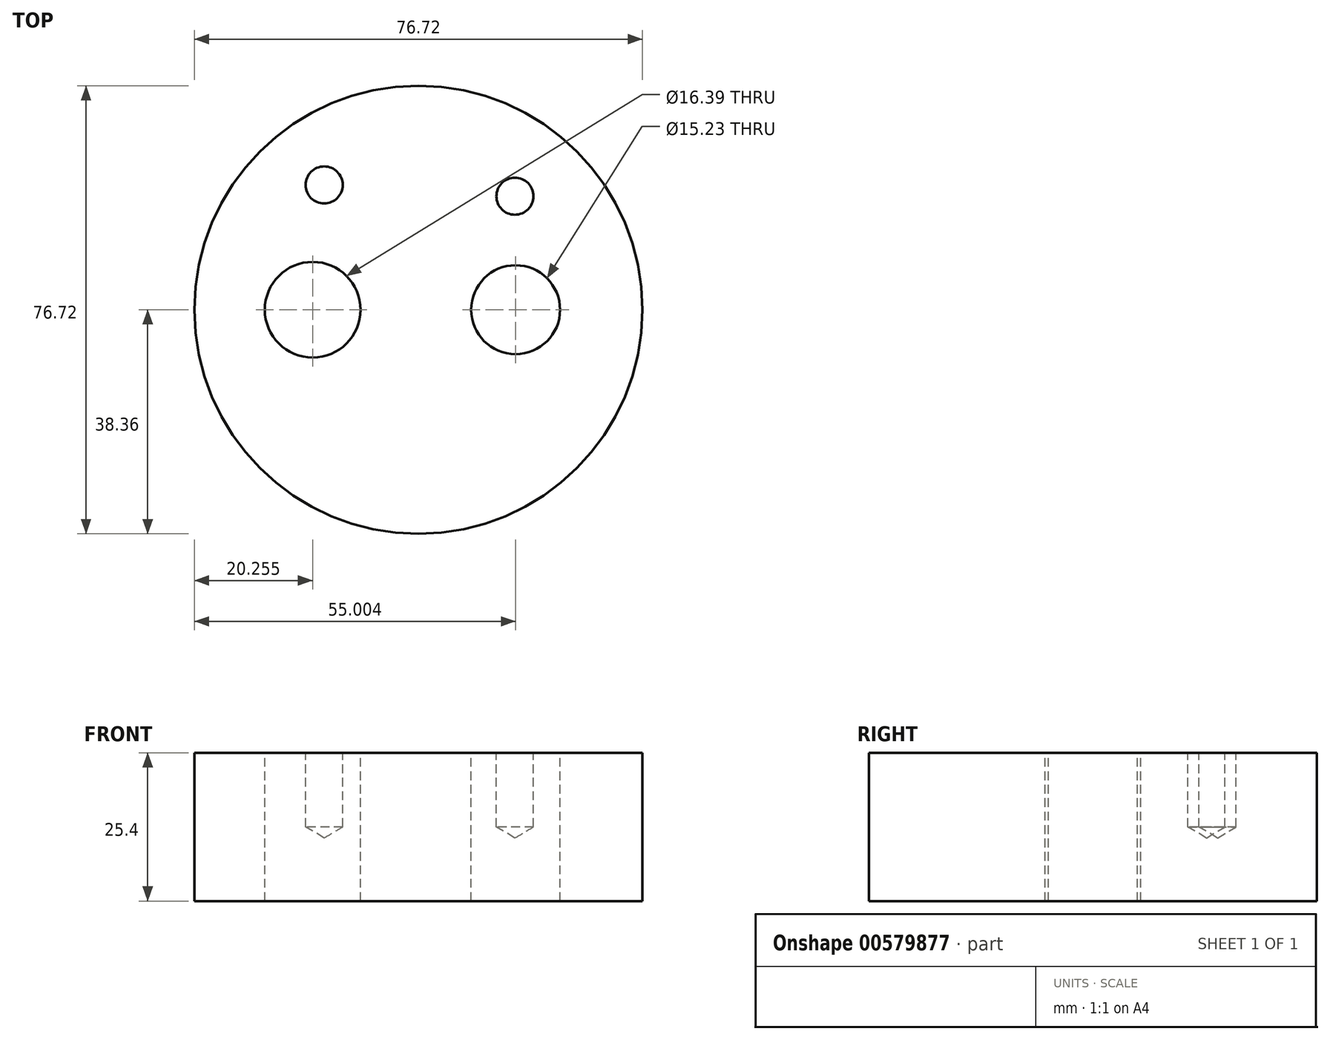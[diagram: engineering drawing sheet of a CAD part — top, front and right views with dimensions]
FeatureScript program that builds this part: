
annotation { "Feature Type Name" : "Feature", "Feature Type Description" : "" }
export const myFeature = defineFeature(function(context is Context, id is Id, definition is map)
    precondition{}
    {
        {
            var Q0;
            Q0=qCreatedBy(makeId("Top.planeOp"),FACE);
            var sketch = newSketch(context, id + "F0", { "sketchPlane" : qUnion([Q0])});
            skCircle(sketch, "E0", {"center": v(0, 0) * mm, "radius": 38.36 * mm});
            skSolve(sketch);
        }
        {
            var Q0;
            Q0 = qSketchRegion(id + "F0", true);
            extrude(context, id + "F1", {"entities" : qUnion([Q0]), "depth" : 25.4 * mm, "offsetDistance" : 25.4 * mm});
        }
        {
            var Q0;
            Q0=makeQuery(id+"F1.opExtrude","CAP_FACE",FACE,{"disambiguationData":[OSD([sQuery(id+"F0.wireOp",EDGE,"E0")])],"isStart":false});
            var sketch = newSketch(context, id + "F2", { "sketchPlane" : qUnion([Q0])});
            skCircle(sketch, "E1", {"center": v(-18.1, 0) * mm, "radius": 8.2 * mm});
            skCircle(sketch, "E2", {"center": v(16.64, 0) * mm, "radius": 7.61 * mm});
            skSolve(sketch);
        }
        {
            var Q0;
            Q0=makeQuery(id+"F2.imprint","IMPRINT",FACE,{"disambiguationData":[TD([[makeQuery(id+"F2.imprint","IMPRINT",EDGE,{"derivedFrom":sQuery(id+"F2.wireOp",EDGE,"E2")}),1.0]])]});
            var Q1;
            Q1=makeQuery(id+"F2.imprint","IMPRINT",FACE,{"disambiguationData":[TD([[makeQuery(id+"F2.imprint","IMPRINT",EDGE,{"derivedFrom":sQuery(id+"F2.wireOp",EDGE,"E1")}),1.0]])]});
            extrude(context, id + "F3", {"entities" : qUnion([Q0, Q1]), "operationType" : NewBodyOperationType.REMOVE, "endBound" : BoundingType.THROUGH_ALL, "oppositeDirection" : true, "depth" : 25.4 * mm, "offsetDistance" : 25.4 * mm});
        }
        {
            var Q0;
            Q0=makeQuery(id+"F1.opExtrude","CAP_FACE",FACE,{"disambiguationData":[OSD([sQuery(id+"F0.wireOp",EDGE,"E0")])],"isStart":false});
            var sketch = newSketch(context, id + "F4", { "sketchPlane" : qUnion([Q0])});
            skCircle(sketch, "E3", {"center": v(0, 0) * mm, "radius": 4.78 * mm});
            skCircle(sketch, "E4", {"center": v(-2.2, 0) * mm, "radius": 0.87 * mm});
            skCircle(sketch, "E5", {"center": v(2.25, 0) * mm, "radius": 0.85 * mm});
            skCircle(sketch, "E6", {"center": v(0, 0) * mm, "radius": 24.12 * mm});
            skArc(sketch, "E7", {"start": v(-11.17, 21.37) * mm, "mid": v(-19.13, 25.33) * mm, "end": v(-17.5, 16.6) * mm});
            skArc(sketch, "E8", {"start": v(19.06, 14.77) * mm, "mid": v(19.98, 23.5) * mm, "end": v(11.5, 21.2) * mm});
            skSolve(sketch);
        }
        {
            var Q0;
            Q0=sQuery(id+"F4.wireOp",VERTEX,"E7.center");
            var Q1;
            Q1=sQuery(id+"F4.wireOp",VERTEX,"E8.center");
            var Q2;
            Q2=makeQuery(id+"F1.opExtrude","SWEPT_BODY",BODY,{"disambiguationData":[OSD([sQuery(id+"F0.wireOp",EDGE,"E0")])]});
            hole(context, id + "F5", {"style" : HoleStyle.SIMPLE, "endStyle" : HoleEndStyle.BLIND, "holeDiameter" : 6.35 * mm, "holeDepth" : 12.7 * mm, "isTappedThrough" : true, "tappedDepth" : 12.7 * mm, "tapClearance" : 3, "locations" : qUnion([Q0, Q1]), "scope" : qUnion([Q2])});
        }
    });
